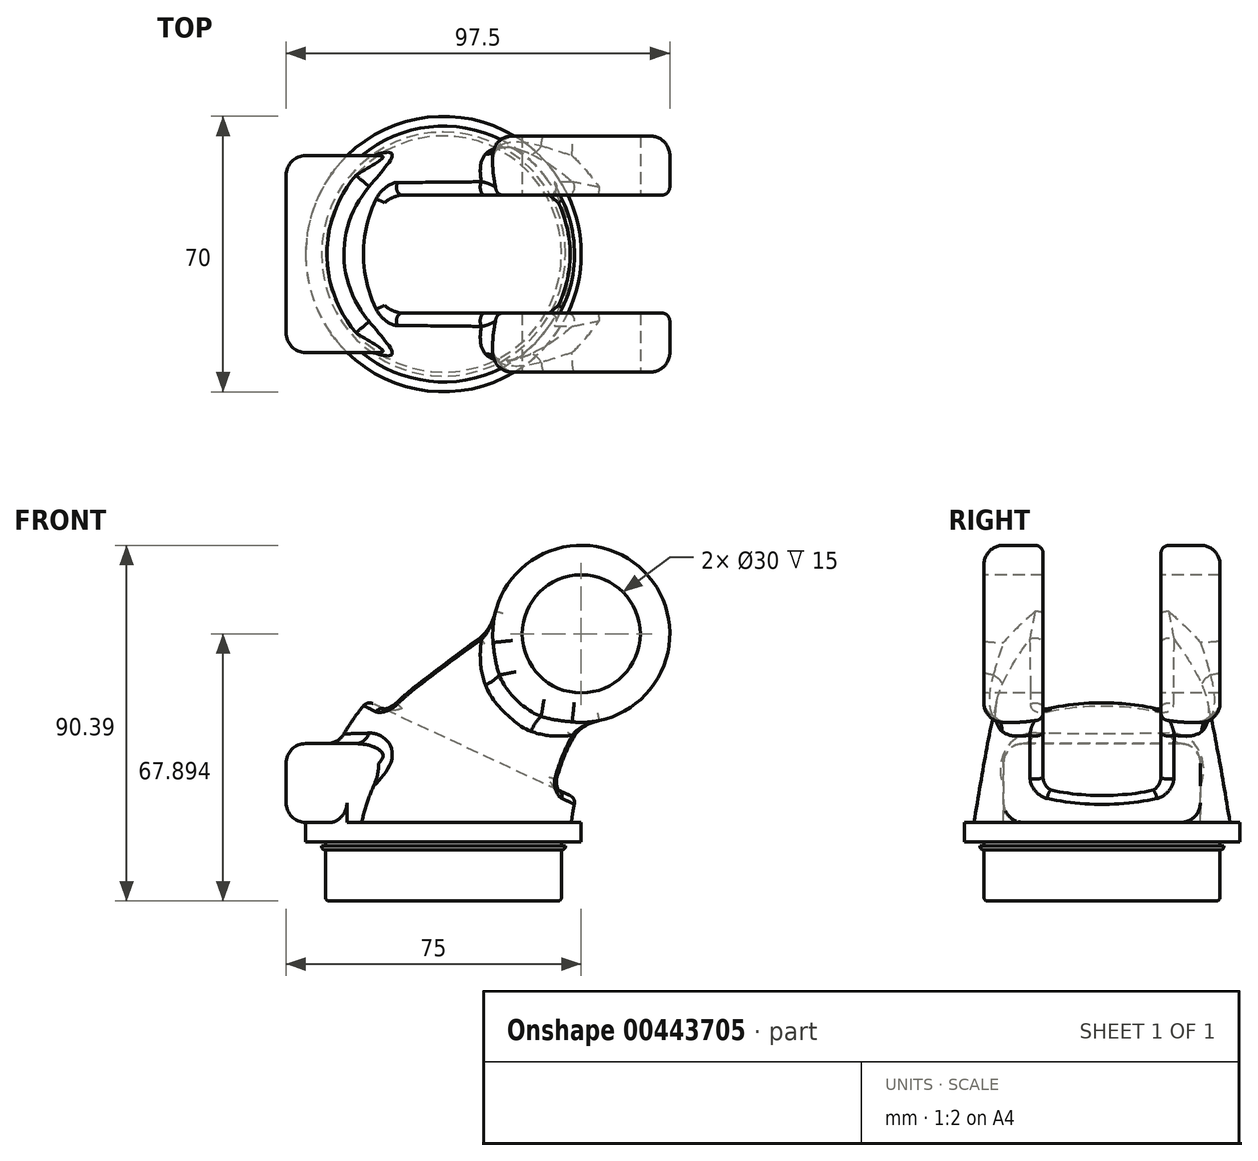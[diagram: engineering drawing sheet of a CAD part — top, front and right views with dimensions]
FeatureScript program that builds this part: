
annotation { "Feature Type Name" : "Feature", "Feature Type Description" : "" }
export const myFeature = defineFeature(function(context is Context, id is Id, definition is map)
    precondition{}
    {
        {
            var Q0;
            Q0=qCreatedBy(makeId("Top.planeOp"),FACE);
            var sketch = newSketch(context, id + "F0", { "sketchPlane" : qUnion([Q0])});
            skCircle(sketch, "E0", {"center": v(0, 0) * mm, "radius": 35 * mm});
            skSolve(sketch);
        }
        {
            var Q0;
            Q0=makeQuery(id+"F0.imprint","IMPRINT",FACE,{"disambiguationData":[TD([[makeQuery(id+"F0.imprint","IMPRINT",EDGE,{"derivedFrom":sQuery(id+"F0.wireOp",EDGE,"E0")}),1.0]])]});
            extrude(context, id + "F1", {"entities" : qUnion([Q0]), "depth" : 5 * mm});
        }
        {
            var Q0;
            Q0=qCreatedBy(makeId("Front.planeOp"),FACE);
            var sketch = newSketch(context, id + "F2", { "sketchPlane" : qUnion([Q0])});
            skArc(sketch, "E1", {"start": v(17.6, 38.3) * mm, "mid": v(5.55, 23.37) * mm, "end": v(0, 5) * mm});
            skLineSegment(sketch, "E2", {"start": v(35, 52.9) * mm, "end": v(17.6, 38.3) * mm});
            skSolve(sketch);
        }
        {
            var Q0;
            Q0=sQuery(id+"F2.wireOp",EDGE,"E2");
            var Q1;
            Q1=sQuery(id+"F2.wireOp",VERTEX,"E2.start");
            cPlane(context, id + "F3", {"entities" : qUnion([Q0, Q1]), "cplaneType" : CPlaneType.LINE_POINT, "offset" : 25 * mm, "width" : 150 * mm, "height" : 150 * mm});
        }
        {
            var Q0;
            Q0=qCreatedBy(id+"F3.planeOp",FACE);
            var sketch = newSketch(context, id + "F4", { "sketchPlane" : qUnion([Q0])});
            skCircle(sketch, "E3", {"center": v(0, 18.02) * mm, "radius": 22.5 * mm});
            skSolve(sketch);
        }
        {
            var Q0;
            Q0=makeQuery(id+"F1.opExtrude","CAP_FACE",FACE,{"disambiguationData":[OSD([sQuery(id+"F0.wireOp",EDGE,"E0")])],"isStart":false});
            var sketch = newSketch(context, id + "F5", { "sketchPlane" : qUnion([Q0])});
            skCircle(sketch, "E4", {"center": v(0, 0) * mm, "radius": 32.5 * mm});
            skSolve(sketch);
        }
        {
            var Q0;
            Q0=qCreatedBy(makeId("Front.planeOp"),FACE);
            var sketch = newSketch(context, id + "F6", { "sketchPlane" : qUnion([Q0])});
            skArc(sketch, "E5", {"start": v(-13.25, 41.78) * mm, "mid": v(-26.5, 25.3) * mm, "end": v(-32.5, 5) * mm});
            skLineSegment(sketch, "E6", {"start": v(-13.25, 41.78) * mm, "end": v(20.54, 70.13) * mm});
            skSolve(sketch);
        }
        {
            var Q0;
            Q0=qCreatedBy(makeId("Front.planeOp"),FACE);
            var sketch = newSketch(context, id + "F7", { "sketchPlane" : qUnion([Q0])});
            skArc(sketch, "E7", {"start": v(48.46, 34.82) * mm, "mid": v(37.6, 21.45) * mm, "end": v(32.5, 5) * mm});
            skLineSegment(sketch, "E8", {"start": v(48.46, 34.82) * mm, "end": v(49.46, 35.66) * mm});
            skSolve(sketch);
        }
        {
            var Q1;
            Q1=makeQuery(id+"F4.imprint","IMPRINT",FACE,{"disambiguationData":[TD([[makeQuery(id+"F4.imprint","IMPRINT",EDGE,{"derivedFrom":sQuery(id+"F4.wireOp",EDGE,"E3")}),1.0]])]});
            var Q2;
            Q2=makeQuery(id+"F5.imprint","IMPRINT",FACE,{"disambiguationData":[TD([[makeQuery(id+"F5.imprint","IMPRINT",EDGE,{"derivedFrom":sQuery(id+"F5.wireOp",EDGE,"E4")}),1.0]])]});
            var Q3;
            Q3 = qConstructionFilter(qBodyType(qCreatedBy(id + "F6" ,EDGE), BodyType.WIRE), ConstructionObject.NO);
            var Q4;
            Q4 = qConstructionFilter(qBodyType(qCreatedBy(id + "F7" ,EDGE), BodyType.WIRE), ConstructionObject.NO);
            loft(context, id + "F8", {"operationType" : NewBodyOperationType.ADD, "addGuides" : true, "sheetProfilesArray" : [{ "sheetProfileEntities" : qUnion([Q1]) }, { "sheetProfileEntities" : qUnion([Q2]) }], "guidesArray" : [{ "guideEntities" : qUnion([Q3]), "guideDerivativeType" : LoftGuideDerivativeType.DEFAULT, "guideDerivativeMagnitude" : 1 }, { "guideEntities" : qUnion([Q4]), "guideDerivativeType" : LoftGuideDerivativeType.DEFAULT, "guideDerivativeMagnitude" : 1 }]});
        }
        {
            var Q0;
            Q0=qCreatedBy(makeId("Front.planeOp"),FACE);
            var sketch = newSketch(context, id + "F9", { "sketchPlane" : qUnion([Q0])});
            skCircle(sketch, "E9", {"center": v(35, 52.9) * mm, "radius": 22.5 * mm});
            skSolve(sketch);
        }
        {
            var Q0;
            Q0 = qSketchRegion(id + "F9", true);
            extrude(context, id + "F10", {"entities" : qUnion([Q0]), "operationType" : NewBodyOperationType.ADD, "endBound" : BoundingType.SYMMETRIC, "depth" : 60 * mm});
        }
        {
            var Q0;
            Q0=makeQuery(id+"F10.boolean.opBoolean","INTERSECT",EDGE,{"disambiguationData":[OD(0.0)],"derivedFrom":[makeQuery(id+"F8.opLoft","SWEPT_FACE",FACE,{"disambiguationData":[OSD([sQuery(id+"F4.wireOp",EDGE,"E3"),sQuery(id+"F5.wireOp",EDGE,"E4"),sQuery(id+"F6.wireOp",VERTEX,"E6.start"),sQuery(id+"F6.wireOp",EDGE,"E5"),sQuery(id+"F6.wireOp",EDGE,"E6"),sQuery(id+"F7.wireOp",VERTEX,"E8.start"),sQuery(id+"F7.wireOp",EDGE,"E7"),sQuery(id+"F7.wireOp",EDGE,"E8")])]}),makeQuery(id+"F10.opExtrude","SWEPT_FACE",FACE,{"disambiguationData":[OSD([sQuery(id+"F9.wireOp",EDGE,"E9")])]})]});
            var Q1;
            Q1=makeQuery(id+"F10.boolean.opBoolean","INTERSECT",EDGE,{"disambiguationData":[OD(1.0)],"derivedFrom":[makeQuery(id+"F8.opLoft","SWEPT_FACE",FACE,{"disambiguationData":[OSD([sQuery(id+"F4.wireOp",EDGE,"E3"),sQuery(id+"F5.wireOp",EDGE,"E4"),sQuery(id+"F6.wireOp",VERTEX,"E6.start"),sQuery(id+"F6.wireOp",EDGE,"E5"),sQuery(id+"F6.wireOp",EDGE,"E6"),sQuery(id+"F7.wireOp",VERTEX,"E8.start"),sQuery(id+"F7.wireOp",EDGE,"E7"),sQuery(id+"F7.wireOp",EDGE,"E8")])]}),makeQuery(id+"F10.opExtrude","SWEPT_FACE",FACE,{"disambiguationData":[OSD([sQuery(id+"F9.wireOp",EDGE,"E9")])]})]});
            fillet(context, id + "F11", {"entities" : qUnion([Q0, Q1]), "radius" : 5 * mm, "tangentPropagation" : true, "allowEdgeOverflow" : false});
        }
        {
            var Q0;
            Q0=makeQuery(id+"F10.opExtrude","CAP_EDGE",EDGE,{"disambiguationData":[OSD([sQuery(id+"F9.wireOp",EDGE,"E9")])],"isStart":false});
            var Q1;
            Q1=makeQuery(id+"F10.opExtrude","CAP_FACE",FACE,{"disambiguationData":[OSD([sQuery(id+"F9.wireOp",EDGE,"E9")])],"isStart":true});
            fillet(context, id + "F12", {"entities" : qUnion([Q0, Q1]), "radius" : 5 * mm, "tangentPropagation" : true, "allowEdgeOverflow" : false});
        }
        {
            var Q0;
            Q0=makeQuery(id+"F10.opExtrude","CAP_FACE",FACE,{"disambiguationData":[OSD([sQuery(id+"F9.wireOp",EDGE,"E9")])],"isStart":false});
            var sketch = newSketch(context, id + "F13", { "sketchPlane" : qUnion([Q0])});
            skCircle(sketch, "E10", {"center": v(35, 52.9) * mm, "radius": 15 * mm});
            skSolve(sketch);
        }
        {
            var Q0;
            Q0 = qSketchRegion(id + "F13", true);
            extrude(context, id + "F14", {"entities" : qUnion([Q0]), "operationType" : NewBodyOperationType.REMOVE, "endBound" : BoundingType.THROUGH_ALL, "oppositeDirection" : true, "depth" : 25 * mm});
        }
        {
            var Q0;
            Q0=qCreatedBy(makeId("Front.planeOp"),FACE);
            var sketch = newSketch(context, id + "F15", { "sketchPlane" : qUnion([Q0])});
            skLineSegment(sketch, "E11", {"start": v(-104.18, 75.4) * mm, "end": v(57.5, 0) * mm});
            skLineSegment(sketch, "E12", {"start": v(57.5, 75.4) * mm, "end": v(57.5, 0) * mm});
            skLineSegment(sketch, "E13", {"start": v(-104.18, 75.4) * mm, "end": v(57.5, 75.4) * mm});
            skSolve(sketch);
        }
        {
            var Q0;
            Q0=makeQuery(id+"F15.imprint","IMPRINT",FACE,{"disambiguationData":[TD([[makeQuery(id+"F15.imprint","IMPRINT",EDGE,{"derivedFrom":sQuery(id+"F15.wireOp",EDGE,"E11")}),1.0]])]});
            extrude(context, id + "F16", {"entities" : qUnion([Q0]), "operationType" : NewBodyOperationType.REMOVE, "endBound" : BoundingType.SYMMETRIC, "oppositeDirection" : true, "depth" : 30 * mm});
        }
        {
            var Q0;
            Q0=qCreatedBy(makeId("Front.planeOp"),FACE);
            var sketch = newSketch(context, id + "F17", { "sketchPlane" : qUnion([Q0])});
            skLineSegment(sketch, "E14.bottom", {"start": v(0, 0) * mm, "end": v(-30, 0) * mm});
            skLineSegment(sketch, "E14.top", {"start": v(0, -15) * mm, "end": v(-30, -15) * mm});
            skLineSegment(sketch, "E14.left", {"start": v(0, 0) * mm, "end": v(0, -15) * mm});
            skLineSegment(sketch, "E15", {"start": v(-30, 0) * mm, "end": v(-30, -1) * mm});
            skLineSegment(sketch, "E16", {"start": v(-30, -1) * mm, "end": v(-31, -1) * mm});
            skLineSegment(sketch, "E17", {"start": v(-31, -1) * mm, "end": v(-31, -2) * mm});
            skLineSegment(sketch, "E18", {"start": v(-31, -2) * mm, "end": v(-30, -2) * mm});
            skLineSegment(sketch, "E19", {"start": v(-30, -2) * mm, "end": v(-30, -15) * mm});
            skSolve(sketch);
        }
        {
            var Q0;
            Q0=makeQuery(id+"F17.imprint","IMPRINT",FACE,{"disambiguationData":[TD([[makeQuery(id+"F17.imprint","IMPRINT",EDGE,{"derivedFrom":sQuery(id+"F17.wireOp",EDGE,"E14.bottom")}),1.0]])]});
            var Q1;
            Q1=sQuery(id+"F17.wireOp",EDGE,"E14.left");
            revolve(context, id + "F18", {"operationType" : NewBodyOperationType.ADD, "entities" : qUnion([Q0]), "axis" : qUnion([Q1]), "revolveType" : RevolveType.FULL});
        }
        {
            var Q0;
            Q0=qCreatedBy(makeId("Right.planeOp"),FACE);
            var sketch = newSketch(context, id + "F19", { "sketchPlane" : qUnion([Q0])});
            skLineSegment(sketch, "E20.bottom", {"start": v(25, 25) * mm, "end": v(-25, 25) * mm});
            skLineSegment(sketch, "E20.top", {"start": v(25, 5) * mm, "end": v(-25, 5) * mm});
            skLineSegment(sketch, "E20.left", {"start": v(25, 25) * mm, "end": v(25, 5) * mm});
            skLineSegment(sketch, "E20.right", {"start": v(-25, 25) * mm, "end": v(-25, 5) * mm});
            skSolve(sketch);
        }
        {
            var Q0;
            Q0 = qSketchRegion(id + "F19", true);
            extrude(context, id + "F20", {"entities" : qUnion([Q0]), "operationType" : NewBodyOperationType.ADD, "oppositeDirection" : true, "depth" : 40 * mm});
        }
        {
            var Q0;
            Q0=makeQuery(id+"F20.boolean.opBoolean","INTERSECT",EDGE,{"derivedFrom":[makeQuery(id+"F8.opLoft","SWEPT_FACE",FACE,{"disambiguationData":[OSD([sQuery(id+"F4.wireOp",EDGE,"E3"),sQuery(id+"F5.wireOp",EDGE,"E4"),sQuery(id+"F6.wireOp",VERTEX,"E6.start"),sQuery(id+"F6.wireOp",EDGE,"E5"),sQuery(id+"F6.wireOp",EDGE,"E6"),sQuery(id+"F7.wireOp",VERTEX,"E8.start"),sQuery(id+"F7.wireOp",EDGE,"E7"),sQuery(id+"F7.wireOp",EDGE,"E8")])]}),makeQuery(id+"F20.opExtrude","SWEPT_FACE",FACE,{"disambiguationData":[OSD([sQuery(id+"F19.wireOp",EDGE,"E20.bottom")])]})]});
            var Q1;
            Q1=makeQuery(id+"F20.opExtrude","SWEPT_EDGE",EDGE,{"disambiguationData":[OSD([sQuery(id+"F19.wireOp",EDGE,"E20.bottom"),sQuery(id+"F19.wireOp",EDGE,"E20.right")])]});
            var Q2;
            Q2=makeQuery(id+"F20.opExtrude","CAP_EDGE",EDGE,{"disambiguationData":[OSD([sQuery(id+"F19.wireOp",EDGE,"E20.bottom")])],"isStart":false});
            var Q3;
            Q3=makeQuery(id+"F20.opExtrude","SWEPT_EDGE",EDGE,{"disambiguationData":[OSD([sQuery(id+"F19.wireOp",EDGE,"E20.bottom"),sQuery(id+"F19.wireOp",EDGE,"E20.left")])]});
            var Q4;
            Q4=makeQuery(id+"F20.opExtrude","CAP_FACE",FACE,{"disambiguationData":[OSD([sQuery(id+"F19.wireOp",EDGE,"E20.bottom"),sQuery(id+"F19.wireOp",EDGE,"E20.top"),sQuery(id+"F19.wireOp",EDGE,"E20.left"),sQuery(id+"F19.wireOp",EDGE,"E20.right")])],"isStart":false});
            var Q5;
            {var subQ0=sQuery(id+"F19.wireOp",EDGE,"E20.top");var subQ1=sQuery(id+"F19.wireOp",EDGE,"E20.right");Q5=makeQuery(id+"F20.boolean.opBoolean","SPLIT",EDGE,{"disambiguationData":[topologyDisambiguationEdgeConnected([makeQuery(id+"F20.opExtrude","SWEPT_FACE",FACE,{"disambiguationData":[OSD([subQ0])]})])],"derivedFrom":makeQuery(id+"F20.opExtrude","SWEPT_EDGE",EDGE,{"disambiguationData":[OSD([subQ0,subQ1])]})});}
            var Q6;
            {var subQ0=sQuery(id+"F19.wireOp",EDGE,"E20.top");var subQ1=sQuery(id+"F19.wireOp",EDGE,"E20.left");Q6=makeQuery(id+"F20.boolean.opBoolean","SPLIT",EDGE,{"disambiguationData":[topologyDisambiguationEdgeConnected([makeQuery(id+"F20.opExtrude","SWEPT_FACE",FACE,{"disambiguationData":[OSD([subQ0])]})])],"derivedFrom":makeQuery(id+"F20.opExtrude","SWEPT_EDGE",EDGE,{"disambiguationData":[OSD([subQ0,subQ1])]})});}
            fillet(context, id + "F21", {"entities" : qUnion([Q0, Q1, Q2, Q3, Q4, Q5, Q6]), "radius" : 5 * mm, "tangentPropagation" : true, "allowEdgeOverflow" : false});
        }
        {
            var Q0;
            Q0=makeQuery(id+"F16.boolean.opBoolean","INTERSECT",EDGE,{"derivedFrom":[makeQuery(id+"F10.opExtrude","SWEPT_FACE",FACE,{"disambiguationData":[OSD([sQuery(id+"F9.wireOp",EDGE,"E9")])]}),makeQuery(id+"F16.opExtrude","CAP_FACE",FACE,{"disambiguationData":[OSD([sQuery(id+"F15.wireOp",EDGE,"E11"),sQuery(id+"F15.wireOp",EDGE,"E12"),sQuery(id+"F15.wireOp",EDGE,"E13")])],"isStart":true})]});
            var Q1;
            Q1=makeQuery(id+"F16.boolean.opBoolean","INTERSECT",EDGE,{"derivedFrom":[makeQuery(id+"F10.opExtrude","SWEPT_FACE",FACE,{"disambiguationData":[OSD([sQuery(id+"F9.wireOp",EDGE,"E9")])]}),makeQuery(id+"F16.opExtrude","CAP_FACE",FACE,{"disambiguationData":[OSD([sQuery(id+"F15.wireOp",EDGE,"E11"),sQuery(id+"F15.wireOp",EDGE,"E12"),sQuery(id+"F15.wireOp",EDGE,"E13")])],"isStart":false})]});
            var Q2;
            Q2=makeQuery(id+"F16.boolean.opBoolean","COPY",FACE,{"derivedFrom":makeQuery(id+"F16.opExtrude","SWEPT_FACE",FACE,{"disambiguationData":[OSD([sQuery(id+"F15.wireOp",EDGE,"E11")])]})});
            fillet(context, id + "F22", {"entities" : qUnion([Q0, Q1, Q2]), "radius" : 2 * mm, "tangentPropagation" : true, "allowEdgeOverflow" : false});
        }
        {
            var Q0;
            Q0=makeQuery(id+"F18.opRevolve","SWEPT_EDGE",EDGE,{"disambiguationData":[OSD([sQuery(id+"F17.wireOp",EDGE,"E17"),sQuery(id+"F17.wireOp",EDGE,"E18")])]});
            var Q1;
            Q1=makeQuery(id+"F18.opRevolve","SWEPT_EDGE",EDGE,{"disambiguationData":[OSD([sQuery(id+"F17.wireOp",EDGE,"E14.top"),sQuery(id+"F17.wireOp",EDGE,"E19")])]});
            fillet(context, id + "F23", {"entities" : qUnion([Q0, Q1]), "radius" : 1 * mm, "tangentPropagation" : true, "allowEdgeOverflow" : false});
        }
    });
